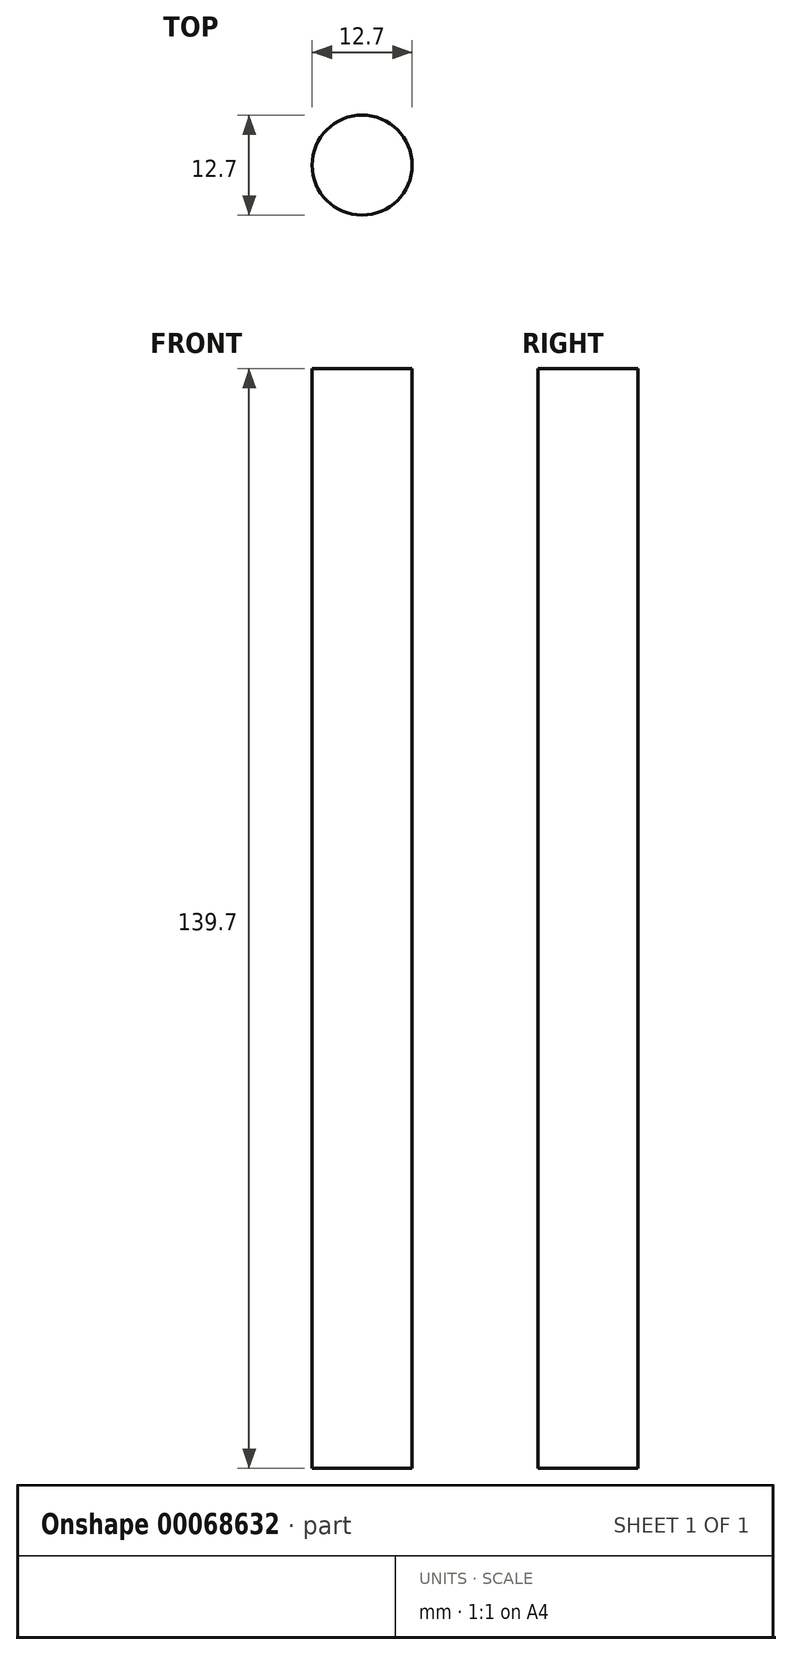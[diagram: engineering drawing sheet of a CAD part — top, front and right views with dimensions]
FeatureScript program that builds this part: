
annotation { "Feature Type Name" : "Feature", "Feature Type Description" : "" }
export const myFeature = defineFeature(function(context is Context, id is Id, definition is map)
    precondition{}
    {
        {
            var Q0;
            Q0=qCreatedBy(makeId("Top.planeOp"),FACE);
            var sketch = newSketch(context, id + "F0", { "sketchPlane" : qUnion([Q0])});
            skCircle(sketch, "E0", {"center": v(0, 0) * mm, "radius": 6.35 * mm});
            skSolve(sketch);
        }
        {
            var Q0;
            Q0=makeQuery(id+"F0.imprint","IMPRINT",FACE,{"disambiguationData":[TD([[makeQuery(id+"F0.imprint","IMPRINT",EDGE,{"derivedFrom":sQuery(id+"F0.wireOp",EDGE,"E0")}),1.0]])]});
            extrude(context, id + "F1", {"entities" : qUnion([Q0]), "depth" : 139.7 * mm});
        }
    });
